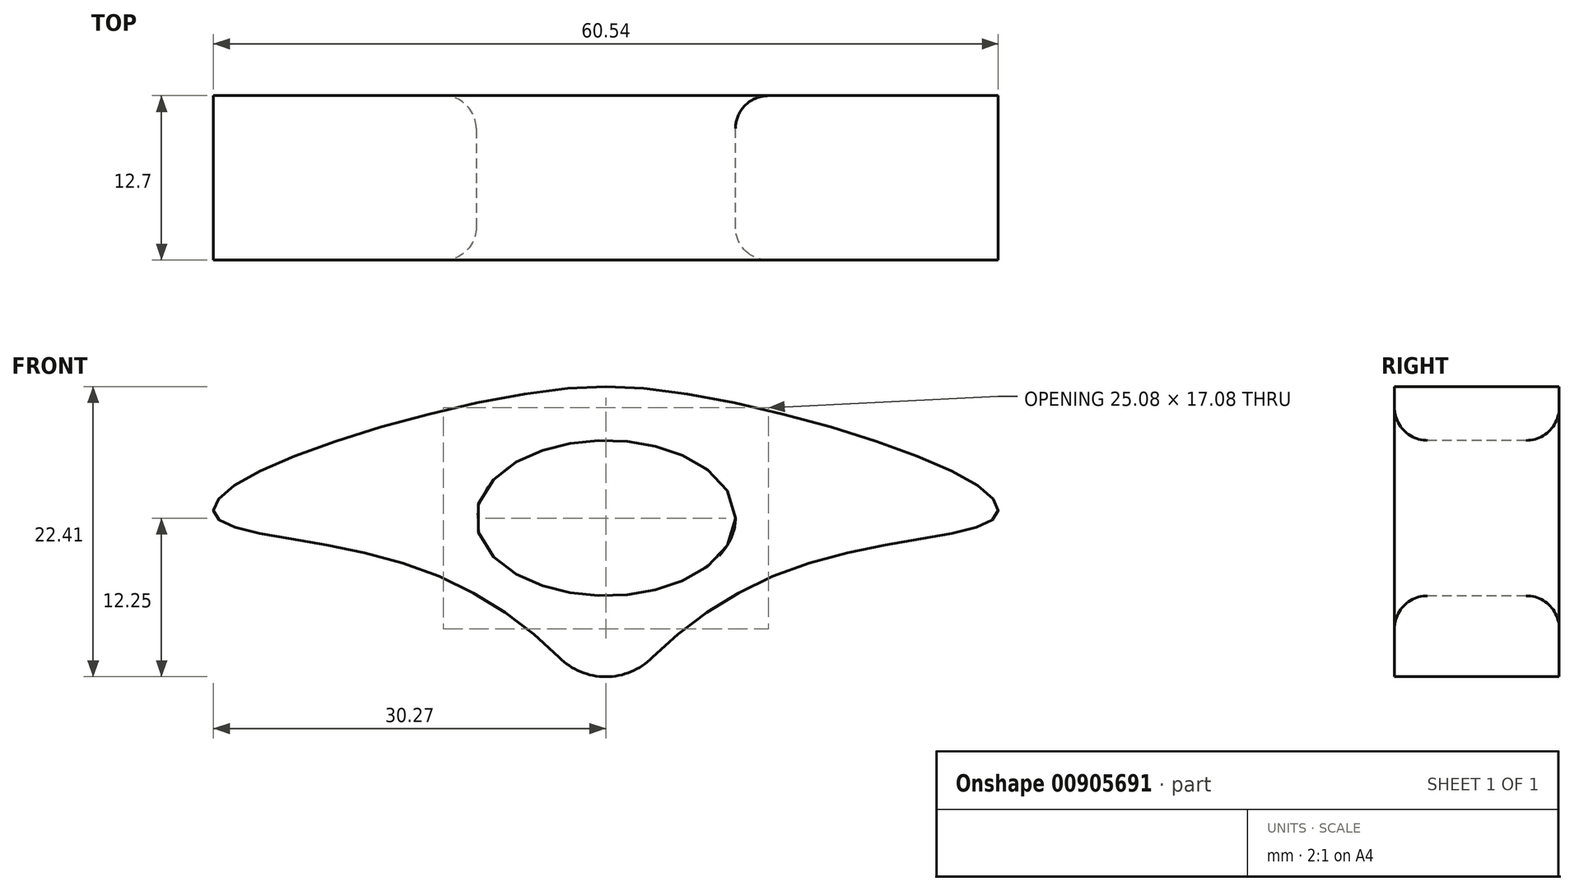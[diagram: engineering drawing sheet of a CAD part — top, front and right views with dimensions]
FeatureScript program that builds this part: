
annotation { "Feature Type Name" : "Feature", "Feature Type Description" : "" }
export const myFeature = defineFeature(function(context is Context, id is Id, definition is map)
    precondition{}
    {
        {
            var Q0;
            Q0=qCreatedBy(makeId("Front.planeOp"),FACE);
            var sketch = newSketch(context, id + "F0", { "sketchPlane" : qUnion([Q0])});
            skLineSegment(sketch, "E0", {"start": v(0, -15.38) * mm, "end": v(5.7, -25.27) * mm, "construction": true});
            skFitSpline(sketch, "E1", {"points": [v(0, -15.38) * mm, v(-14.94, -3.7) * mm, v(-30, 0) * mm, v(-28.61, 2.55) * mm, v(0, 10.16) * mm], "startDerivative": vector(-28.13, 48.73) * mm, "endDerivative": vector(67.97, 0) * mm});
            skLineSegment(sketch, "E2", {"start": v(0, 10.16) * mm, "end": v(10.08, 10.16) * mm, "construction": true});
            skLineSegment(sketch, "E3", {"start": v(0, 0) * mm, "end": v(0, 25.48) * mm, "construction": true});
            skEllipse(sketch, "E4", {"center": v(0, 0) * mm, "majorRadius": 10 * mm, "minorRadius": 6 * mm, "majorAxis": v(1, 0)});
            skLineSegment(sketch, "E5", {"start": v(0, -15.38) * mm, "end": v(0, 10.16) * mm, "construction": true});
            skFitSpline(sketch, "E6.MirrorCS", {"points": [v(0, -15.38) * mm, v(14.94, -3.7) * mm, v(30, 0) * mm, v(28.61, 2.55) * mm, v(0, 10.16) * mm], "startDerivative": vector(28.13, 48.73) * mm, "endDerivative": vector(-67.97, 0) * mm});
            skSolve(sketch);
        }
        {
            var Q0;
            Q0 = qSketchRegion(id + "F0", true);
            var sketch = newSketch(context, id + "F1", { "sketchPlane" : qUnion([Q0])});
            skSolve(sketch);
        }
        {
            var Q0;
            Q0=makeQuery(id+"F1.imprint","IMPRINT",FACE,{"disambiguationData":[TD([[makeQuery(id+"F1.imprint","IMPRINT",EDGE,{"derivedFrom":makeQuery(id+"F0.imprint","IMPRINT",EDGE,{"derivedFrom":sQuery(id+"F0.wireOp",EDGE,"E1")})}),-1.0]])]});
            var Q1;
            Q1=sQuery(id+"F0.wireOp",EDGE,"E1");
            var Q2;
            Q2 = qBodyType(qCreatedBy(id + "F0" ,EDGE), BodyType.WIRE);
            extrude(context, id + "F2", {"entities" : qUnion([Q0]), "surfaceEntities" : qUnion([Q1, Q2]), "depth" : 12.7 * mm, "offsetDistance" : 25.4 * mm});
        }
        {
            var Q0;
            {var subQ0=sQuery(id+"F0.wireOp",EDGE,"E6.MirrorCS");var subQ1=sQuery(id+"F0.wireOp",EDGE,"E1");Q0=makeQuery(id+"F2.opExtrude","SWEPT_EDGE",EDGE,{"disambiguationData":[OSD([subQ1,subQ0]),TDD([makeQuery(id+"F1.imprint","INTERSECT",VERTEX,{"disambiguationData":[OD(0.0)],"derivedFrom":[makeQuery(id+"F0.imprint","IMPRINT",EDGE,{"derivedFrom":subQ1}),makeQuery(id+"F0.imprint","IMPRINT",EDGE,{"derivedFrom":subQ0})]})])]});}
            fillet(context, id + "F3", {"entities" : qUnion([Q0]), "radius" : 5.08 * mm, "tangentPropagation" : true, "allowEdgeOverflow" : false});
        }
        {
            var Q0;
            Q0=makeQuery(id+"F2.opExtrude","CAP_EDGE",EDGE,{"disambiguationData":[OSD([sQuery(id+"F0.wireOp",EDGE,"E4")])],"isStart":false});
            var Q1;
            Q1=makeQuery(id+"F2.opExtrude","CAP_EDGE",EDGE,{"disambiguationData":[OSD([sQuery(id+"F0.wireOp",EDGE,"E4")])],"isStart":true});
            fillet(context, id + "F4", {"entities" : qUnion([Q0, Q1]), "radius" : 2.54 * mm, "tangentPropagation" : true, "allowEdgeOverflow" : false});
        }
    });
